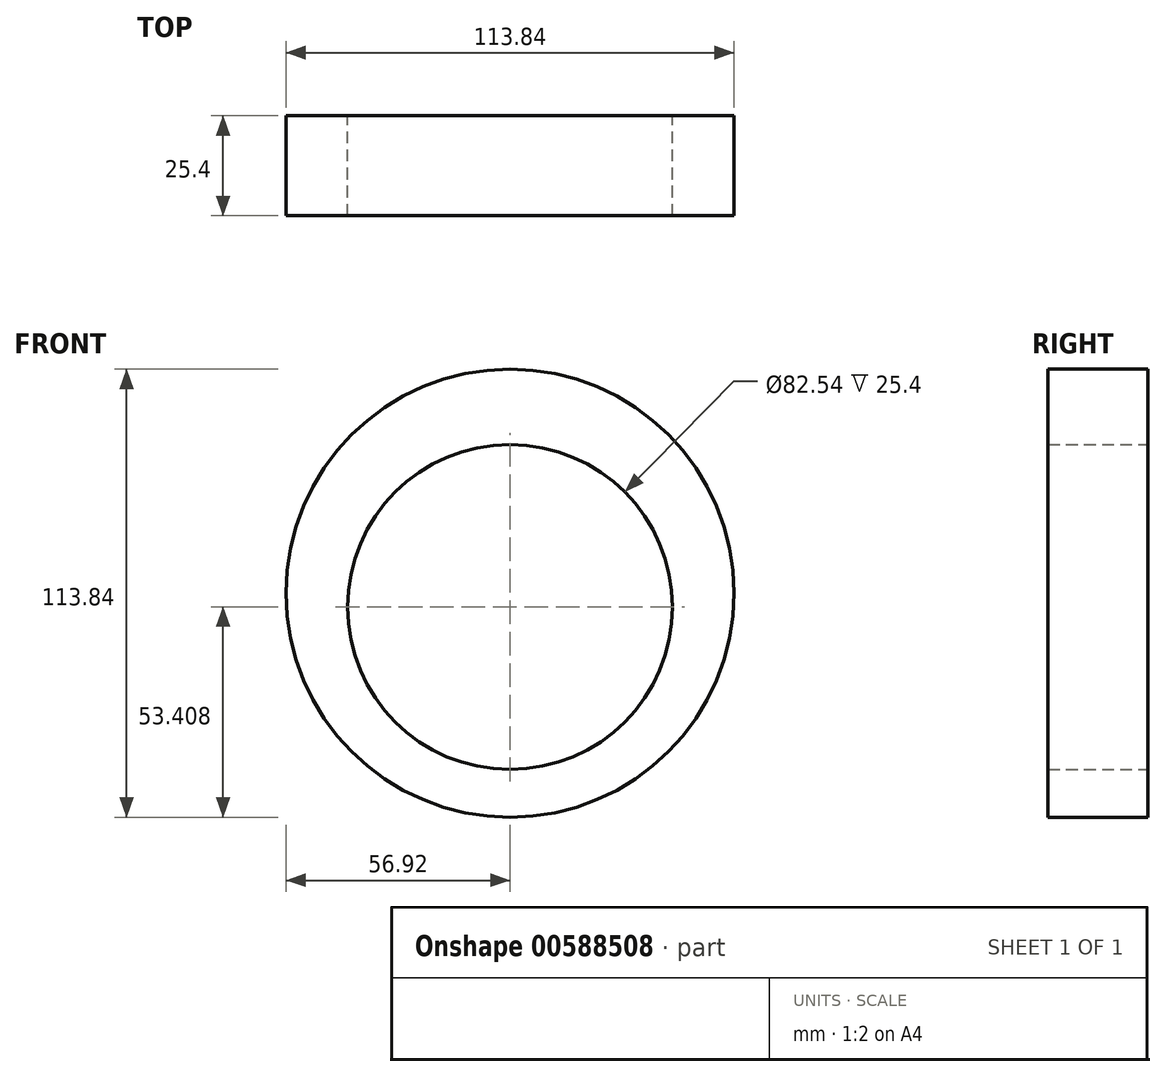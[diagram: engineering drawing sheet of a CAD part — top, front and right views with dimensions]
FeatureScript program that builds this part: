
annotation { "Feature Type Name" : "Feature", "Feature Type Description" : "" }
export const myFeature = defineFeature(function(context is Context, id is Id, definition is map)
    precondition{}
    {
        {
            var Q0;
            Q0=qCreatedBy(makeId("Front.planeOp"),FACE);
            var sketch = newSketch(context, id + "F0", { "sketchPlane" : qUnion([Q0])});
            skCircle(sketch, "E0", {"center": v(0, 0) * mm, "radius": 56.92 * mm});
            skCircle(sketch, "E1", {"center": v(0, -3.51) * mm, "radius": 41.27 * mm});
            skSolve(sketch);
        }
        {
            var Q0;
            Q0=makeQuery(id+"F0.imprint","IMPRINT",FACE,{"disambiguationData":[TD([[makeQuery(id+"F0.imprint","IMPRINT",EDGE,{"derivedFrom":sQuery(id+"F0.wireOp",EDGE,"E0")}),1.0]])]});
            extrude(context, id + "F1", {"entities" : qUnion([Q0]), "depth" : 25.4 * mm, "offsetDistance" : 25.4 * mm});
        }
    });
